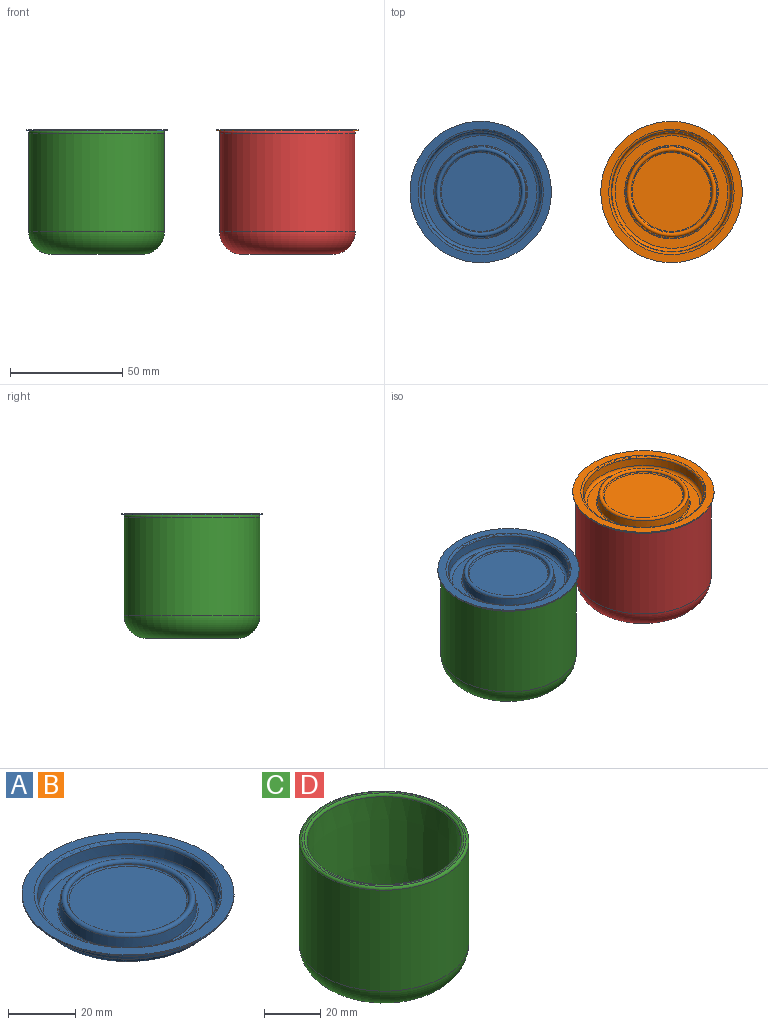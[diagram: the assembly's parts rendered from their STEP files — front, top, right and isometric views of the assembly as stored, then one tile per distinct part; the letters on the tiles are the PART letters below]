
ASSEMBLY  parts=4 mates=5
PART A: 23 faces, bbox 63x63x6.5 mm
  f0: plane 35.08x35.08mm, normal (0,0,-1), area 966.7mm2, adj f18
  f1: cone r=18.46mm half-angle=5deg, axis (0,0,1), area 15.3mm2, adj f2,f18
  f2: torus R=19.05mm, axis (0,0,-1), area 177.5mm2, adj f1,f3
  f3: cone r=19.55mm half-angle=5deg, axis (0,0,-1), area 451.2mm2, adj f2,f17
  f4: plane 50.19x50.19mm, normal (0,0,-1), area 611.1mm2, adj f16,f17
  f5: cone r=26.93mm half-angle=5deg, axis (0,0,1), area 638.9mm2, adj f16,f22
  f6: plane 63x63mm, normal (0,0,-1), area 670.4mm2, adj f7,f22
  f7: cylinder r=31.5mm len=63mm, axis (0,0,-1), area 99mm2, adj f6,f8
  f8: plane 63x63mm, normal (0,0,1), area 670.4mm2, adj f7,f21
  f9: cone r=26.99mm half-angle=5deg, axis (0,0,1), area 627.3mm2, adj f15,f21
  f10: plane 50.19x50.19mm, normal (0,0,1), area 611.1mm2, adj f15,f20
  f11: cone r=20.4mm half-angle=5deg, axis (0,0,-1), area 462.6mm2, adj f12,f20
  f12: torus R=19.05mm, axis (0,0,-1), area 355.1mm2, adj f11,f13
  f13: cone r=18mm half-angle=5deg, axis (0,0,1), area 14.9mm2, adj f12,f19
  f14: plane 35.08x35.08mm, normal (0,0,1), area 966.7mm2, adj f19
  f15: torus R=25.09mm, axis (0,0,1), area 363.7mm2, adj f9,f10
  f16: torus R=25.09mm, axis (0,0,-1), area 490.7mm2, adj f4,f5
  f17: torus R=20.86mm, axis (0,0,-1), area 188.7mm2, adj f3,f4
  f18: torus R=17.54mm, axis (0,0,-1), area 169.2mm2, adj f0,f1
  f19: torus R=17.54mm, axis (0,0,-1), area 83.2mm2, adj f13,f14
  f20: torus R=20.86mm, axis (0,0,1), area 95.8mm2, adj f10,f11
  f21: torus R=27.91mm, axis (0,0,1), area 254.4mm2, adj f8,f9
  f22: torus R=27.91mm, axis (0,0,-1), area 128.6mm2, adj f5,f6
PART B: same geometry as A
PART C: 13 faces, bbox 65.5x65.5x55 mm
  f0: plane 58.5x58.5mm, normal (0,0,1), area 148.1mm2, adj f1,f12
  f1: torus R=28.43mm, axis (0,0,-1), area 271.3mm2, adj f0,f2
  f2: cone r=26.76mm half-angle=1deg, axis (0,0,1), area 6588.1mm2, adj f1,f3
  f3: torus R=16.76mm, axis (0,0,-1), area 2253mm2, adj f2,f4
  f4: plane 33.52x33.52mm, normal (0,0,1), area 882.4mm2, adj f3
  f5: plane 34.55x34.55mm, normal (0,0,-1), area 937.5mm2, adj f6
  f6: torus R=17.28mm, axis (0,0,-1), area 97mm2, adj f5,f7
  f7: cone r=18.7mm half-angle=40deg, axis (0,0,-1), area 118.4mm2, adj f6,f8
  f8: torus R=19.47mm, axis (0,0,-1), area 104.5mm2, adj f7,f9
  f9: plane 40.5x40.5mm, normal (0,0,-1), area 97.8mm2, adj f8,f10
  f10: torus R=20.25mm, axis (0,0,-1), area 2626.9mm2, adj f9,f11
  f11: cylinder r=30.25mm len=60.5mm, axis (0,0,-1), area 8362.9mm2, adj f10,f12
  f12: torus R=29.25mm, axis (0,0,-1), area 295mm2, adj f0,f11
PART D: same geometry as C
PLACE A t=(-5.38,9.64,40.62)mm
PLACE B t=(79.62,9.64,40.62)mm
PLACE C t=(-5.38,9.64,-8.38)mm fixed
PLACE D t=(79.62,9.64,-8.38)mm fixed
MATE planar B.f1 <-> D.f1  axis (0,0,-1) through (79.62,9.64,46.62)mm
MATE planar A.f1 <-> C.f1  axis (0,0,-1) through (-5.38,9.64,46.62)mm
MATE planar D.f1 <-> C.f1  axis (0,0,-1) through (79.62,9.64,-8.38)mm
MATE cylindrical B.f1 <-> D.f1  axis (0,0,1) through (79.62,9.64,47.12)mm
MATE cylindrical A.f1 <-> C.f1  axis (0,0,1) through (-5.38,9.64,47.12)mm
